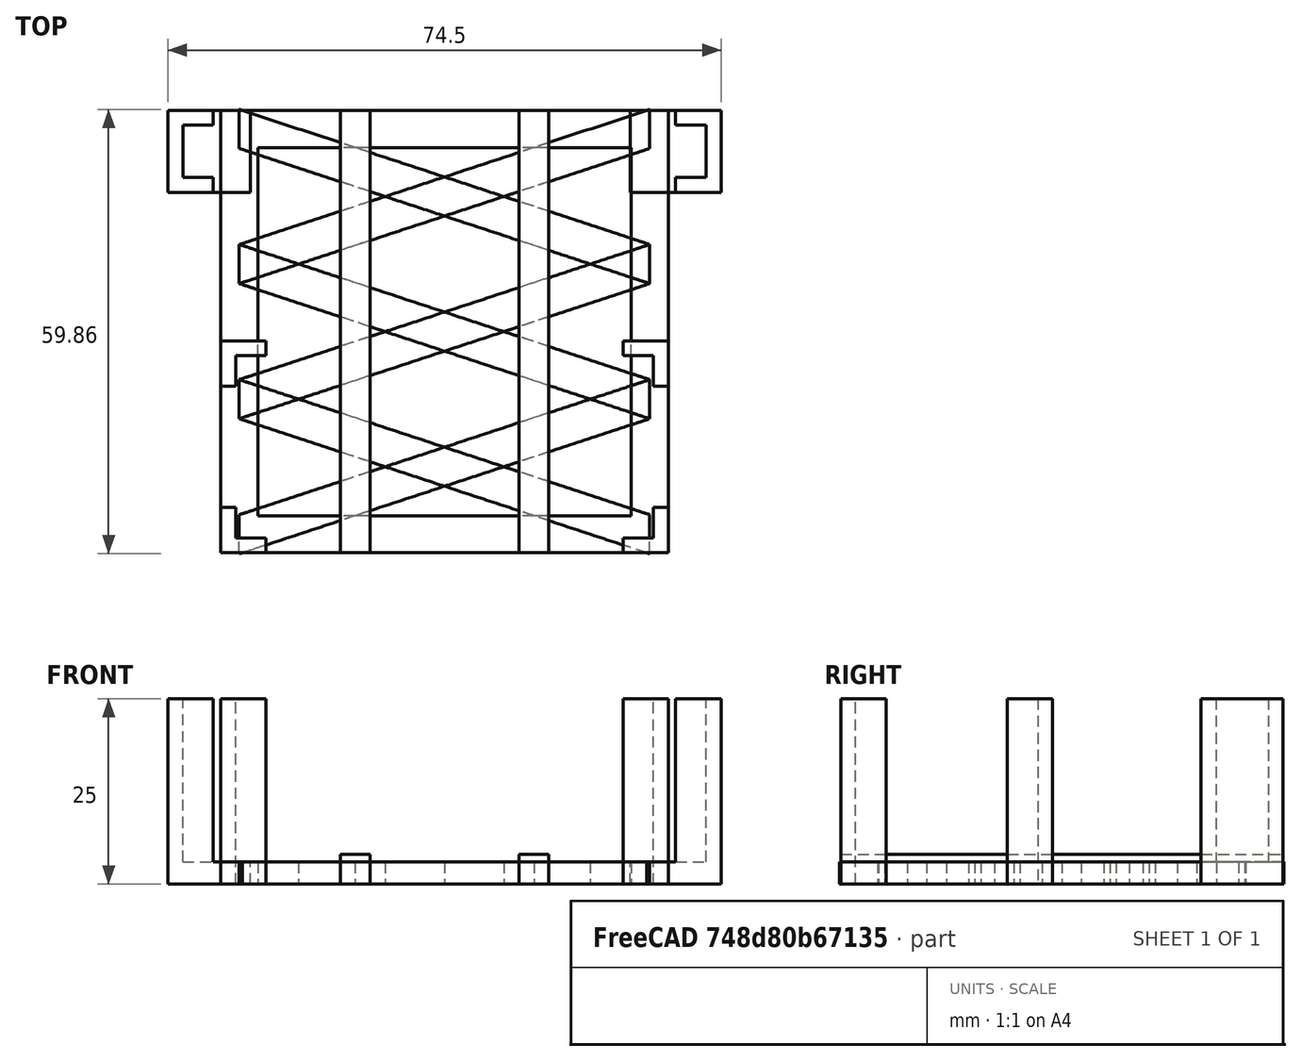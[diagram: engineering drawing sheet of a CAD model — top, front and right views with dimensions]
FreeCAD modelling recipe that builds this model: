
FCSTD DOCUMENT  (FreeCAD 1.0R39109 (Git))
Label: pi_ssd_vertical1
License: All rights reserved
LicenseURL: https://en.wikipedia.org/wiki/All_rights_reserved
objects: Part::Box×11, Part::Plane×8, Part::Feature×7, Part::Fuse×6, Part::Cut×3, Part::MultiFuse×3, Part::FeaturePython×1, Part::Extrusion×1
note: 40 computed .brp shape members not serialized (recipe doc carries the construction recipe); baked Part::Feature solids carry a one-line shape summary decoded from their .brp

FEATURE [Part::Plane] square
  AttacherType = Attacher::AttachEngine3D
  Length = 60.3
  Placement = pos=(-30.15,-29.8,0) rot=(0,0,1;0rad)
  Width = 59.6
FEATURE [Part::Plane] square001
  AttacherType = Attacher::AttachEngine3D
  Length = 50.3
  Placement = pos=(-25.15,-24.8,0) rot=(0,0,1;0rad)
  Width = 49.6
FEATURE [Part::Cut] difference
  Base = -> square
  Refine = true
  Tool = -> square001
FEATURE [Part::Plane] square002
  AttacherType = Attacher::AttachEngine3D
  Length = 55.3
  Placement = pos=(-27.65,-2.63191,0) rot=(0,0,1;0rad)
  Width = 5.26383
FEATURE [Part::Feature] Matrix_Deformation
  Placement = pos=(-27.65,-2.63191,0) rot=(0,0,1;0rad)
  shape: bbox 55.3 x 23.46 x 2e-07 mm, 1 faces, 0 solids (baked)
FEATURE [Part::Plane] square003
  AttacherType = Attacher::AttachEngine3D
  Length = 55.3
  Placement = pos=(-27.65,-2.63191,0) rot=(0,0,1;0rad)
  Width = 5.26383
FEATURE [Part::Feature] Matrix_Deformation001
  Placement = pos=(-27.65,-2.63191,0) rot=(0,0,1;0rad)
  shape: bbox 55.3 x 23.46 x 2e-07 mm, 1 faces, 0 solids (baked)
FEATURE [Part::Fuse] Group
  Base = -> Matrix_Deformation
  Placement = pos=(0,-18.2,0) rot=(0,0,1;0rad)
  Refine = true
  Tool = -> Matrix_Deformation001
FEATURE [Part::Plane] square004
  AttacherType = Attacher::AttachEngine3D
  Length = 55.3
  Placement = pos=(-27.65,-2.63191,0) rot=(0,0,1;0rad)
  Width = 5.26383
FEATURE [Part::Feature] Matrix_Deformation002
  Placement = pos=(-27.65,-2.63191,0) rot=(0,0,1;0rad)
  shape: bbox 55.3 x 23.46 x 2e-07 mm, 1 faces, 0 solids (baked)
FEATURE [Part::Plane] square005
  AttacherType = Attacher::AttachEngine3D
  Length = 55.3
  Placement = pos=(-27.65,-2.63191,0) rot=(0,0,1;0rad)
  Width = 5.26383
FEATURE [Part::Feature] Matrix_Deformation003
  Placement = pos=(-27.65,-2.63191,0) rot=(0,0,1;0rad)
  shape: bbox 55.3 x 23.46 x 2e-07 mm, 1 faces, 0 solids (baked)
FEATURE [Part::Fuse] Group001
  Base = -> Matrix_Deformation002
  Refine = true
  Tool = -> Matrix_Deformation003
FEATURE [Part::Plane] square006
  AttacherType = Attacher::AttachEngine3D
  Length = 55.3
  Placement = pos=(-27.65,-2.63191,0) rot=(0,0,1;0rad)
  Width = 5.26383
FEATURE [Part::Feature] Matrix_Deformation004
  Placement = pos=(-27.65,-2.63191,0) rot=(0,0,1;0rad)
  shape: bbox 55.3 x 23.46 x 2e-07 mm, 1 faces, 0 solids (baked)
FEATURE [Part::Plane] square007
  AttacherType = Attacher::AttachEngine3D
  Length = 55.3
  Placement = pos=(-27.65,-2.63191,0) rot=(0,0,1;0rad)
  Width = 5.26383
FEATURE [Part::Feature] Matrix_Deformation005
  Placement = pos=(-27.65,-2.63191,0) rot=(0,0,1;0rad)
  shape: bbox 55.3 x 23.46 x 2e-07 mm, 1 faces, 0 solids (baked)
FEATURE [Part::Fuse] Group002
  Base = -> Matrix_Deformation004
  Placement = pos=(0,18.2,0) rot=(0,0,1;0rad)
  Refine = true
  Tool = -> Matrix_Deformation005
FEATURE [Part::MultiFuse] Group003
  Refine = true
  Shapes = -> [Group,Group001,Group002]
FEATURE [Part::Fuse] union
  Base = -> difference
  Refine = true
  Tool = -> Group003
FEATURE [Part::FeaturePython] RefineLinearExtrude  # WARN: FeaturePython — macro-defined, semantics opaque (R4)
  Base = -> union
FEATURE [Part::Extrusion] LinearExtrude
  Base = -> RefineLinearExtrude
  Dir = (0,0,3)
  DirMode = 0
  FaceMakerClass = Part::FaceMakerBullseye
  FaceMakerMode = 3
  LengthFwd = 0
  LengthRev = 0
  Placement = pos=(30.15,0,1.5) rot=(0,1,0;3.14159rad)
  Solid = false
  Symmetric = false
FEATURE [Part::Box] cube
  AttacherType = Attacher::AttachEngine3D
  Height = 4
  Length = 4
  Placement = pos=(16.1,-29.8,-1.5) rot=(0,0,1;0rad)
  Width = 59.6
FEATURE [Part::Box] cube001
  AttacherType = Attacher::AttachEngine3D
  Height = 4
  Length = 4
  Placement = pos=(40.2,-29.8,-1.5) rot=(0,0,1;0rad)
  Width = 59.6
FEATURE [Part::Box] cube002
  AttacherType = Attacher::AttachEngine3D
  Height = 25
  Length = 74.5
  Width = 11.05
FEATURE [Part::Box] cube003
  AttacherType = Attacher::AttachEngine3D
  Height = 25
  Length = 70.5
  Placement = pos=(2,2,0) rot=(0,0,1;0rad)
  Width = 7.05
FEATURE [Part::Feature] emptycube
  Placement = pos=(0,6.675,0) rot=(0,0,1;0rad)
FEATURE [Part::Box] cube004
  AttacherType = Attacher::AttachEngine3D
  Height = 25
  Length = 62.3
  Placement = pos=(6.1,0,0) rot=(0,0,1;0rad)
  Width = 11.05
FEATURE [Part::MultiFuse] union001
  Refine = true
  Shapes = -> [cube003,emptycube,cube004]
FEATURE [Part::Cut] difference001
  Base = -> cube002
  Refine = true
  Tool = -> union001
FEATURE [Part::Box] cube005
  AttacherType = Attacher::AttachEngine3D
  Height = 3
  Length = 11.1
  Width = 11.05
FEATURE [Part::Box] cube006
  AttacherType = Attacher::AttachEngine3D
  Height = 3
  Length = 11.1
  Placement = pos=(62.3,0,0) rot=(0,0,1;0rad)
  Width = 11.05
FEATURE [Part::Fuse] Group004
  Base = -> cube005
  Refine = true
  Tool = -> cube006
FEATURE [Part::Fuse] Group005
  Base = -> difference001
  Placement = pos=(-7.1,18.75,-1.5) rot=(0,0,1;0rad)
  Refine = true
  Tool = -> Group004
FEATURE [Part::Box] cube007
  AttacherType = Attacher::AttachEngine3D
  Height = 25
  Length = 60.3
  Width = 28.55
FEATURE [Part::Box] cube008
  AttacherType = Attacher::AttachEngine3D
  Height = 25
  Length = 56.3
  Placement = pos=(2,2,0) rot=(0,0,1;0rad)
  Width = 24.55
FEATURE [Part::Box] cube009
  AttacherType = Attacher::AttachEngine3D
  Height = 25
  Length = 60.3
  Placement = pos=(0,6.1,0) rot=(0,0,1;0rad)
  Width = 16.35
FEATURE [Part::Box] cube010
  AttacherType = Attacher::AttachEngine3D
  Height = 25
  Length = 48.1
  Placement = pos=(6.1,0,0) rot=(0,0,1;0rad)
  Width = 28.55
FEATURE [Part::MultiFuse] union002
  Refine = true
  Shapes = -> [cube008,cube009,cube010]
FEATURE [Part::Cut] difference002
  Base = -> cube007
  Placement = pos=(0,-29.8,-1.5) rot=(0,0,1;0rad)
  Refine = true
  Tool = -> union002
